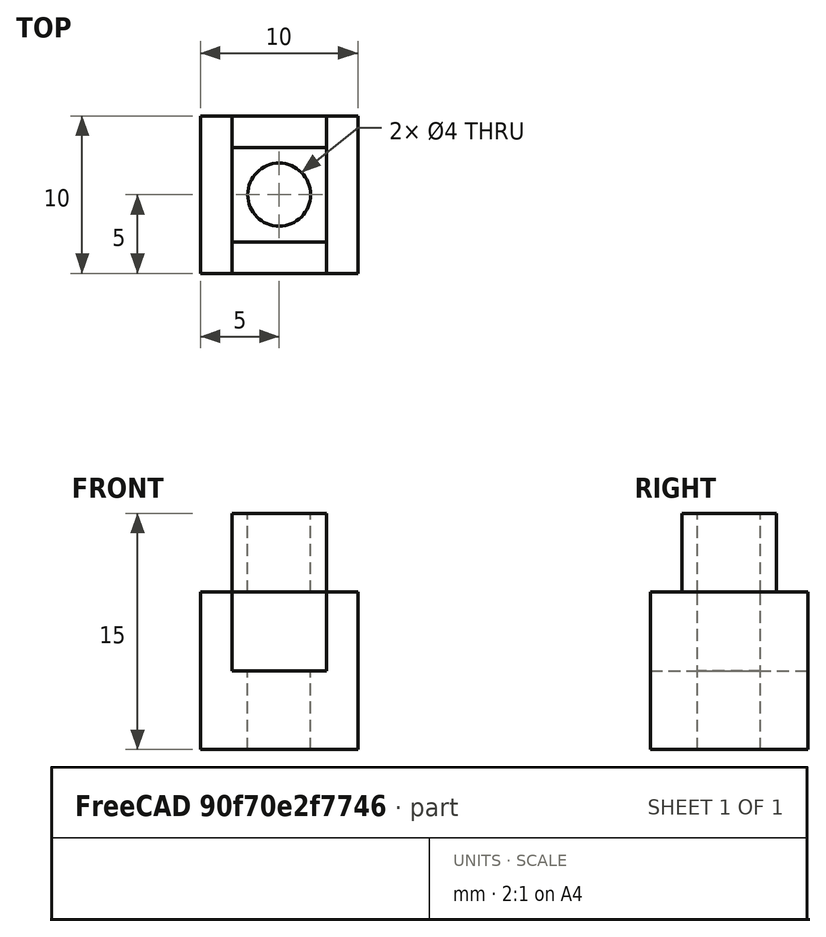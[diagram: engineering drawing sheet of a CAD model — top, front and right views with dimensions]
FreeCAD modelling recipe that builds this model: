
FCSTD DOCUMENT  (FreeCAD 0.19R24291 (Git))
Label: STL2CSG-test-objects
License: All rights reserved
LicenseURL: http://en.wikipedia.org/wiki/All_rights_reserved
objects: Part::Box×6, Part::Cut×3, Part::Cylinder×3, Part::MultiFuse×2
note: 14 computed .brp shape members not serialized (recipe doc carries the construction recipe); baked Part::Feature solids carry a one-line shape summary decoded from their .brp

FEATURE [Part::Box] Box  label="Cube"
  AttacherType = Attacher::AttachEngine3D
  Height = 10
  Length = 10
  Width = 10
FEATURE [Part::Box] Box001  label="Cube001"
  AttacherType = Attacher::AttachEngine3D
  Height = 10
  Length = 6
  Placement = pos=(2,-1,5) rot=(0,0,1;0rad)
  Width = 14
FEATURE [Part::Cut] Cut
  Base = -> Box
  Tool = -> Box001
FEATURE [Part::Cylinder] Cylinder
  Angle = 360
  AttacherType = Attacher::AttachEngine3D
  Height = 10
  Placement = pos=(5,5,-1) rot=(0,0,1;0rad)
  Radius = 2
FEATURE [Part::Cut] Cut001  label="woo-1"
  Base = -> Cut
  Tool = -> Cylinder
FEATURE [Part::Box] Box002  label="Cube002"
  AttacherType = Attacher::AttachEngine3D
  Height = 10
  Length = 10
  Width = 10
FEATURE [Part::Box] Box003  label="Cube003"
  AttacherType = Attacher::AttachEngine3D
  Height = 10
  Length = 6
  Placement = pos=(2,2,5) rot=(0,0,1;0rad)
  Width = 6
FEATURE [Part::MultiFuse] Fusion  label="woo-2"
  Shapes = -> [Box002,Box003]
FEATURE [Part::Box] Box004  label="Cube004"
  AttacherType = Attacher::AttachEngine3D
  Height = 10
  Length = 10
  Width = 10
FEATURE [Part::Cylinder] Cylinder001
  Angle = 360
  AttacherType = Attacher::AttachEngine3D
  Height = 12
  Placement = pos=(5,5,-1) rot=(0,0,1;0rad)
  Radius = 2
FEATURE [Part::Cut] Cut002  label="cube-cylinder"
  Base = -> Box004
  Tool = -> Cylinder001
FEATURE [Part::Box] Box005  label="Cube005"
  AttacherType = Attacher::AttachEngine3D
  Height = 10
  Length = 10
  Width = 10
FEATURE [Part::Cylinder] Cylinder002
  Angle = 360
  AttacherType = Attacher::AttachEngine3D
  Height = 12
  Placement = pos=(5,5,3) rot=(0,0,1;0rad)
  Radius = 2
FEATURE [Part::MultiFuse] Fusion001  label="cubePlusCylinder"
  Shapes = -> [Box005,Cylinder002]
